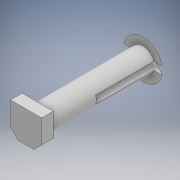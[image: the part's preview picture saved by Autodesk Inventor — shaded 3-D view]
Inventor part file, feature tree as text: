
AUTODESK INVENTOR PART (.ipt)
format: ipt  version: 2018 (Build 220112000, 112)  size: 162,304 bytes
history: native  units: mm
features: sketch x5, extrude x4, other x1, revolve x1
ambient origin geometry x8: Origin, YZ Plane, XZ Plane, XY Plane, X Axis, Y Axis, Z Axis, Center Point
bodies: Body1 (feature_tree), Body2 (feature_tree), Body3 (feature_tree), Body4 (feature_tree)
feature tree (11):
  other  "Sólido1"
  revolve  "Revolución1"  [1 undecoded]
  extrude  "Extrusión1"  TaperAngle=90.0deg  [1 undecoded]
  extrude  "Extrusión2"  Depth=4.0mm
  extrude  "Extrusión3"  Depth=8.0mm
  extrude  "Extrusión4"  Depth=15.0mm TaperAngle=0.0deg
  sketch  "Boceto1"  dims[d0=3.0mm d1=27.0mm]
  sketch  "Boceto2"  dims[d2=5.0mm d4=90.0deg]
  sketch  "Boceto4"  dims[d5=4.0mm d6=4.0mm]
  sketch  "Boceto5"  dims[d7=8.0mm d8=8.0mm]
  sketch  "Boceto6"  dims[d9=2.0mm d10=3.0mm d11=0.0mm d15=15.0mm d16=180.0deg d17=1.0mm d18=1.0mm d19=7.0mm d20=0.0mm d21=7.0mm d22=0.0mm d23=2.0mm d24=20.0mm d25=0.0mm]
note: 2 required parameter values undecoded (feature->parameter linkage not recoverable at this tier; creation-order binding heuristic only, values carry confidence <= 0.55)